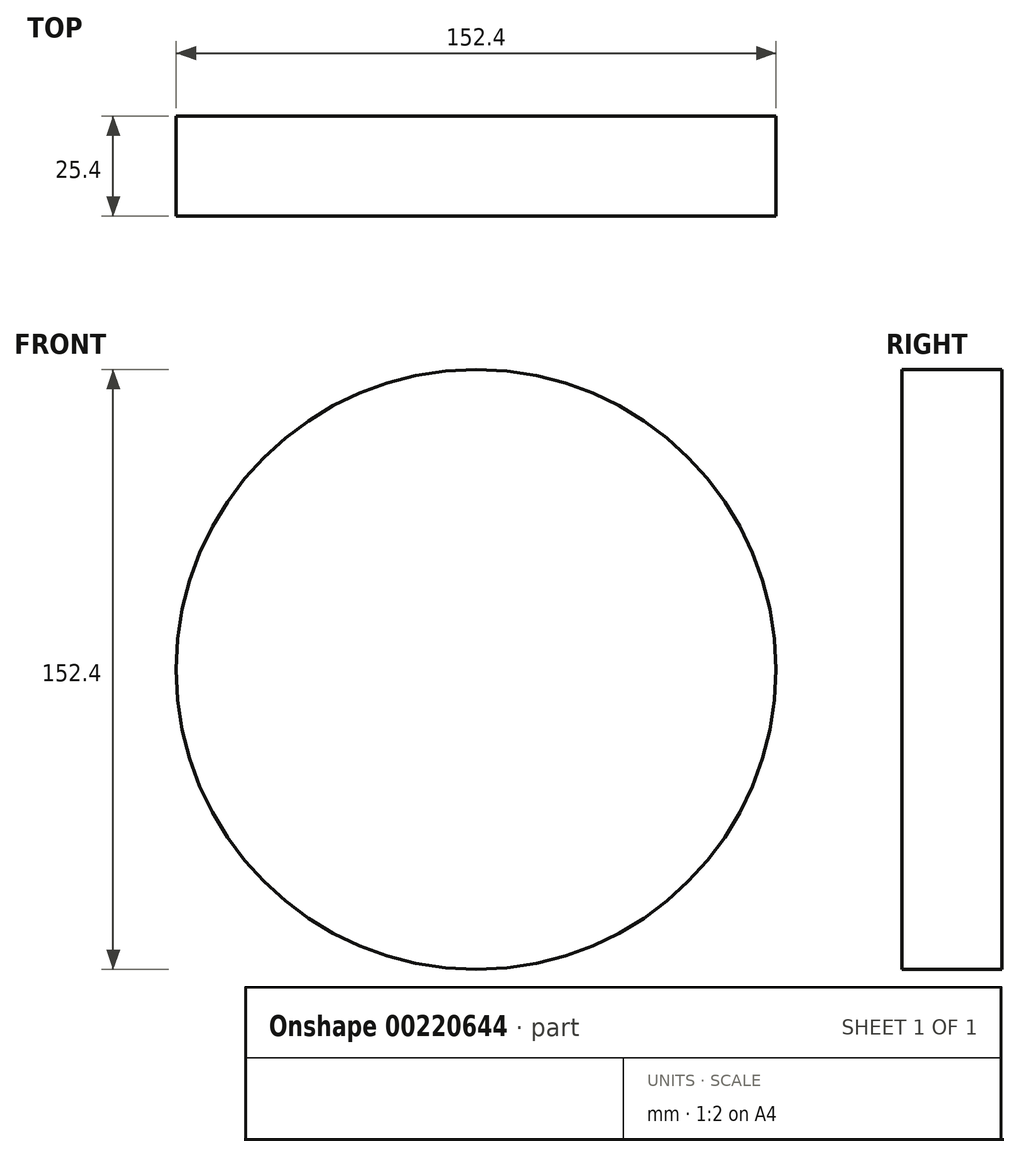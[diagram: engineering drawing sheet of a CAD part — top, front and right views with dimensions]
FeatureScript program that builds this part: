
annotation { "Feature Type Name" : "Feature", "Feature Type Description" : "" }
export const myFeature = defineFeature(function(context is Context, id is Id, definition is map)
    precondition{}
    {
        {
            var Q0;
            Q0=qCreatedBy(makeId("Front.planeOp"),FACE);
            var sketch = newSketch(context, id + "F0", { "sketchPlane" : qUnion([Q0])});
            skCircle(sketch, "E0", {"center": v(0, 0) * mm, "radius": 82 * mm, "construction": true});
            skCircle(sketch, "E1", {"center": v(0, 0) * mm, "radius": 95.18 * mm, "construction": true});
            skCircle(sketch, "E2", {"center": v(0, 0) * mm, "radius": 76.2 * mm});
            skLineSegment(sketch, "E3", {"start": v(0, 0) * mm, "end": v(0, 109.87) * mm, "construction": true});
            skLineSegment(sketch, "E4", {"start": v(0, 0) * mm, "end": v(-25.64, 106.94) * mm, "construction": true});
            skLineSegment(sketch, "E5", {"start": v(0, 82) * mm, "end": v(-106.89, 82) * mm, "construction": true});
            skLineSegment(sketch, "E6", {"start": v(0, 82) * mm, "end": v(-100.68, 42) * mm, "construction": true});
            skCircle(sketch, "E7", {"center": v(0, 82) * mm, "radius": 31.66 * mm, "construction": true});
            skCircle(sketch, "E8", {"center": v(0, 0) * mm, "radius": 76.2 * mm, "construction": true});
            skSolve(sketch);
        }
        {
            var Q0;
            Q0=makeQuery(id+"F0.imprint","IMPRINT",FACE,{"disambiguationData":[TD([[makeQuery(id+"F0.imprint","IMPRINT",EDGE,{"derivedFrom":sQuery(id+"F0.wireOp",EDGE,"E2")}),1.0]])]});
            extrude(context, id + "F1", {"entities" : qUnion([Q0]), "depth" : 25.4 * mm});
        }
    });
